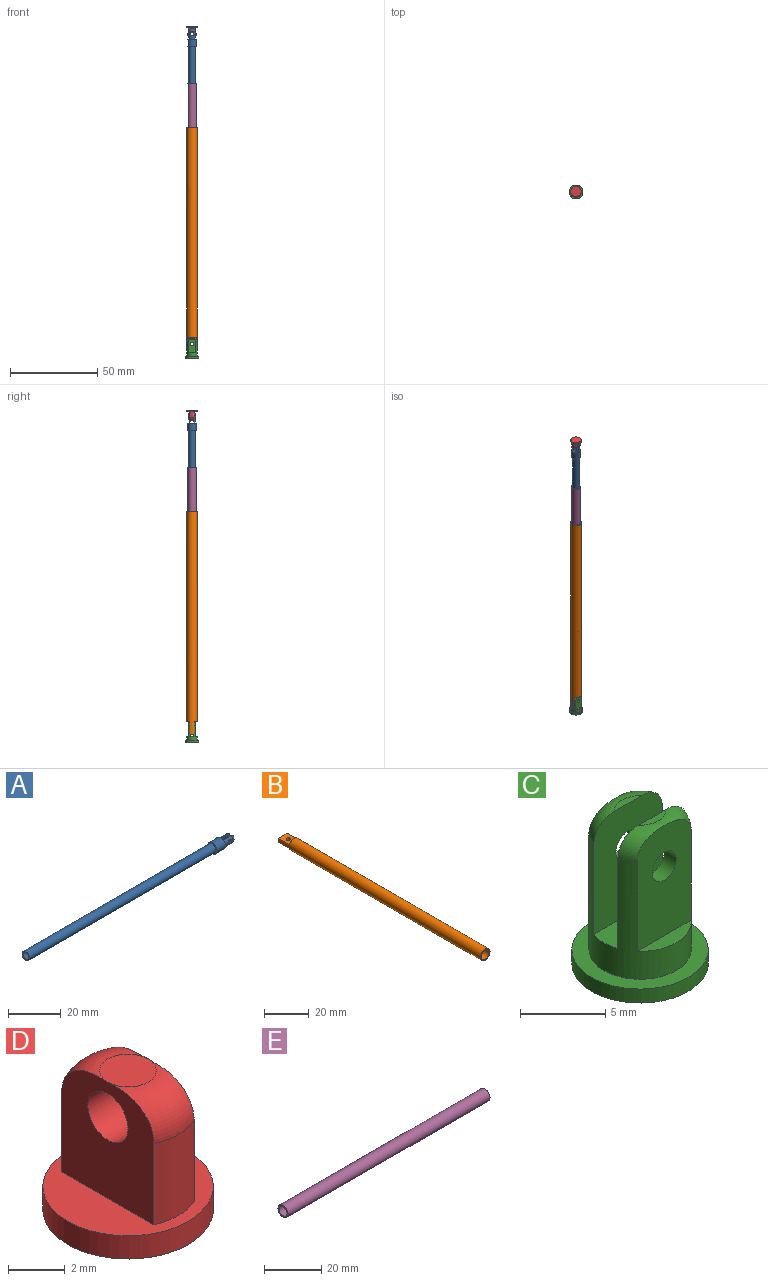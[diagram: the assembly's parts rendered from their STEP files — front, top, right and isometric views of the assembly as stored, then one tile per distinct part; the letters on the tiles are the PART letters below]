
ASSEMBLY  parts=5 mates=4
PART A: 15 faces, bbox 110.4x5x5 mm
  f0: cylinder r=2mm len=4.5mm, axis (-1,0,0), area 15.6mm2, adj f4,f8,f9,f12
  f1: cylinder r=2mm len=100mm, axis (-1,0,0), area 1256.6mm2, adj f2,f5
  f2: plane 4x4mm, normal (-1,0,0), area 5.5mm2, adj f1,f13
  f3: cylinder r=2.5mm len=5mm, axis (-1,0,0), area 70.7mm2, adj f4,f5
  f4: plane 5x5mm, normal (1,0,0), area 14.7mm2, adj f0,f3,f6,f7,f8
  f5: plane 5x5mm, normal (-1,0,0), area 7.1mm2, adj f1,f3
  f6: cylinder r=2mm len=4.5mm, axis (-1,0,0), area 15.6mm2, adj f4,f7,f10,f11
  f7: plane 5.92x3.46mm, normal (0,1,0), area 16.4mm2, adj f4,f6,f10,f11
  f8: plane 5.92x3.46mm, normal (0,-1,0), area 16.4mm2, adj f0,f4,f9,f12
  f9: cylinder r=1mm len=2mm, axis (0,-1,0), area 5.5mm2, adj f0,f8
  f10: cylinder r=1mm len=2mm, axis (0,-1,0), area 5.5mm2, adj f6,f7
  f11: torus R=0.5mm, axis (1,0,0), area 5.5mm2, adj f6,f7
  f12: torus R=0.5mm, axis (1,0,0), area 5.5mm2, adj f0,f8
  f13: cylinder r=1.5mm len=99mm, axis (-1,0,0), area 933.1mm2, adj f2,f14
  f14: plane 3x3mm, normal (-1,0,0), area 7.1mm2, adj f13
PART B: 10 faces, bbox 6x128x6 mm
  f0: cylinder r=3mm len=128mm, axis (0,1,0), area 2309.3mm2, adj f1,f2,f3,f4,f5,f6
  f1: plane 6x2mm, normal (0,1,0), area 11.8mm2, adj f0,f4,f6
  f2: plane 6x6mm, normal (0,-1,0), area 8.6mm2, adj f0,f8
  f3: plane 5.66x2mm, normal (0,1,0), area 8.3mm2, adj f0,f4
  f4: plane 7x5.66mm, normal (0,0,-1), area 36.6mm2, adj f0,f1,f3,f7
  f5: plane 5.66x2mm, normal (0,1,0), area 8.3mm2, adj f0,f6
  f6: plane 7x5.66mm, normal (0,0,1), area 36.6mm2, adj f0,f1,f5,f7
  f7: cylinder r=0.98mm len=2mm, axis (0,0,-1), area 12.3mm2, adj f4,f6
  f8: cylinder r=2.5mm len=110mm, axis (0,-1,0), area 1727.9mm2, adj f2,f9
  f9: plane 5x5mm, normal (0,-1,0), area 19.6mm2, adj f8
PART C: 17 faces, bbox 8x8x11 mm
  f0: cylinder r=3mm len=8.5mm, axis (0,0,-1), area 68.1mm2, adj f4,f6,f7,f8,f9,f10,f11,f12
  f1: plane 2.24x0.5mm, normal (0,0,1), area 0.8mm2, adj f8,f16
  f2: plane 2.24x0.5mm, normal (0,0,1), area 0.8mm2, adj f7,f15
  f3: cylinder r=4mm len=8mm, axis (0,0,-1), area 25.1mm2, adj f4,f5
  f4: plane 8x8mm, normal (0,0,1), area 22mm2, adj f0,f3
  f5: plane 8x8mm, normal (0,0,-1), area 50.3mm2, adj f3
  f6: plane 6x2mm, normal (0,0,1), area 11.8mm2, adj f0,f7,f8
  f7: plane 8x5.66mm, normal (0,-1,0), area 41.1mm2, adj f0,f2,f6,f13,f15
  f8: plane 8x5.66mm, normal (0,1,0), area 41.1mm2, adj f0,f1,f6,f14,f16
  f9: plane 4.47x1mm, normal (0,0,1), area 3.1mm2, adj f0,f10
  f10: plane 7.91x4.47mm, normal (0,-1,0), area 31.1mm2, adj f0,f9,f14,f16
  f11: plane 4.47x1mm, normal (0,0,1), area 3.1mm2, adj f0,f12
  f12: plane 7.91x4.47mm, normal (0,1,0), area 31.1mm2, adj f0,f11,f13,f15
  f13: cylinder r=1mm len=2mm, axis (0,-1,0), area 6.3mm2, adj f7,f12
  f14: cylinder r=1mm len=2mm, axis (0,-1,0), area 6.3mm2, adj f8,f10
  f15: torus R=1.5mm, axis (0,0,1), area 6.5mm2, adj f0,f2,f7,f12
  f16: torus R=1.5mm, axis (0,0,1), area 6.5mm2, adj f0,f1,f8,f10
PART D: 11 faces, bbox 6x6x6 mm
  f0: cylinder r=2.5mm len=3.5mm, axis (0,0,-1), area 7.2mm2, adj f4,f6,f7,f10
  f1: cylinder r=2.5mm len=3.5mm, axis (0,0,-1), area 7.2mm2, adj f4,f6,f7,f9
  f2: plane 2x2mm, normal (0,0,1), area 3.1mm2, adj f9,f10
  f3: cylinder r=3mm len=6mm, axis (0,0,-1), area 18.8mm2, adj f4,f5
  f4: plane 6x6mm, normal (0,0,1), area 18.5mm2, adj f0,f1,f3,f6,f7
  f5: plane 6x6mm, normal (0,0,-1), area 28.3mm2, adj f3
  f6: plane 5x4.58mm, normal (-1,0,0), area 18.7mm2, adj f0,f1,f4,f8,f9,f10
  f7: plane 5x4.58mm, normal (1,0,0), area 18.7mm2, adj f0,f1,f4,f8,f9,f10
  f8: cylinder r=1mm len=2mm, axis (-1,0,0), area 12.6mm2, adj f6,f7
  f9: torus R=1mm, axis (0,0,1), area 5.1mm2, adj f1,f2,f6,f7
  f10: torus R=1mm, axis (0,0,1), area 5.1mm2, adj f0,f2,f6,f7
PART E: 4 faces, bbox 100x5x5 mm
  f0: cylinder r=2mm len=100mm, axis (-1,0,0), area 1256.6mm2, adj f2,f3
  f1: cylinder r=2.5mm len=100mm, axis (-1,0,0), area 1570.8mm2, adj f2,f3
  f2: plane 5x5mm, normal (1,0,0), area 7.1mm2, adj f0,f1
  f3: plane 5x5mm, normal (-1,0,0), area 7.1mm2, adj f0,f1
PLACE A rot(axis=(0,-1,0),90deg) t=(22.43,4.06,94.88)mm
PLACE B rot(axis=(-1,0,0),90deg) t=(22.43,4.06,20.71)mm
PLACE C t=(22.43,4.06,16.21)mm
PLACE D rot(axis=(-0.71,-0.71,0),180deg) t=(22.43,4.06,206.88)mm
PLACE E rot(axis=(-0.71,0,0.71),180deg) t=(22.43,4.06,173.89)mm
MATE slider A.f1 <-> E.f1  axis (0,0,-1) through (22.43,4.06,94.88)mm
MATE revolute B.f7 <-> C.f13  axis (0,1,0) through (22.43,5.06,24.21)mm
MATE slider E.f1 <-> B.f8  axis (0,0,1) through (22.43,4.06,123.89)mm
MATE revolute D.f8 <-> A.f9  axis (0,-1,0) through (22.43,3.06,202.38)mm
